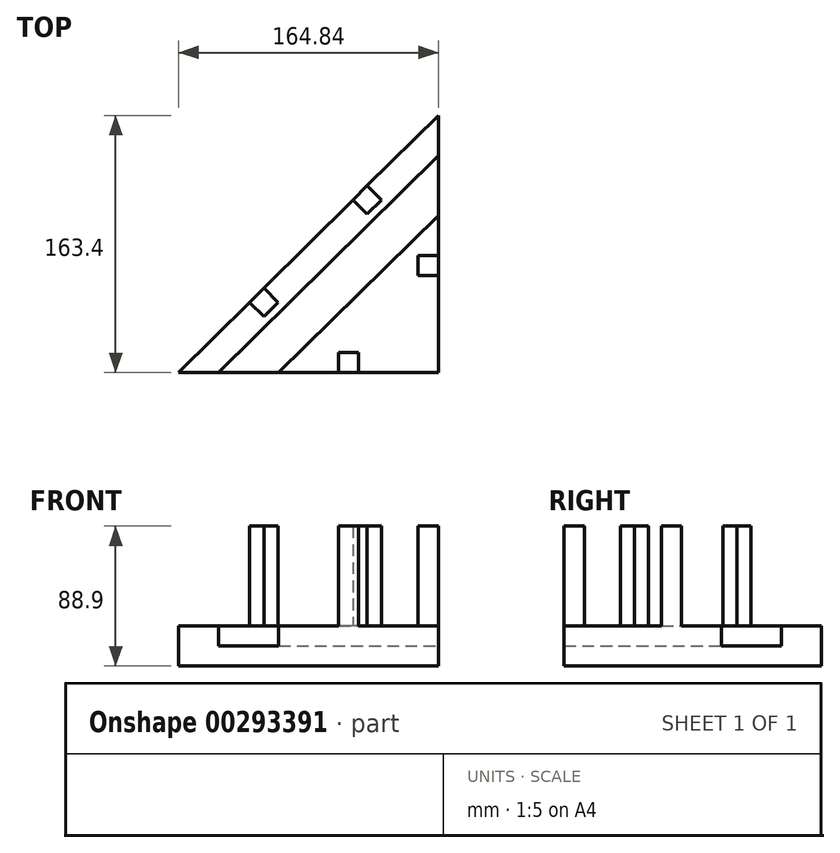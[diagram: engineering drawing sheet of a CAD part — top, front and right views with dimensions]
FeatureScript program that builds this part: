
annotation { "Feature Type Name" : "Feature", "Feature Type Description" : "" }
export const myFeature = defineFeature(function(context is Context, id is Id, definition is map)
    precondition{}
    {
        {
            var Q0;
            Q0=qCreatedBy(makeId("Top.planeOp"),FACE);
            var sketch = newSketch(context, id + "F0", { "sketchPlane" : qUnion([Q0])});
            skLineSegment(sketch, "E0.top", {"start": v(82.42, -81.7) * mm, "end": v(-82.42, -81.7) * mm});
            skLineSegment(sketch, "E0.left", {"start": v(82.42, 81.7) * mm, "end": v(82.42, -81.7) * mm});
            skPoint(sketch, "E0.middle", {"position": v(0, 0) * mm});
            skLineSegment(sketch, "E1", {"start": v(82.42, 81.7) * mm, "end": v(-82.42, -81.7) * mm});
            skSolve(sketch);
        }
        {
            var Q0;
            Q0=makeQuery(id+"F0.imprint","IMPRINT",FACE,{"disambiguationData":[TD([[makeQuery(id+"F0.imprint","IMPRINT",EDGE,{"derivedFrom":sQuery(id+"F0.wireOp",EDGE,"E0.top")}),-1.0]])]});
            extrude(context, id + "F1", {"entities" : qUnion([Q0]), "depth" : 25.4 * mm});
        }
        {
            var Q0;
            Q0=makeQuery(id+"F1.opExtrude","CAP_FACE",FACE,{"disambiguationData":[OSD([sQuery(id+"F0.wireOp",EDGE,"E0.top"),sQuery(id+"F0.wireOp",EDGE,"E0.left"),sQuery(id+"F0.wireOp",EDGE,"E1")])],"isStart":false});
            var sketch = newSketch(context, id + "F2", { "sketchPlane" : qUnion([Q0])});
            skLineSegment(sketch, "E2", {"start": v(-82.42, -81.7) * mm, "end": v(-18.92, -81.7) * mm});
            skLineSegment(sketch, "E3", {"start": v(82.42, 81.7) * mm, "end": v(82.42, 18.2) * mm});
            skLineSegment(sketch, "E4", {"start": v(-18.92, -81.7) * mm, "end": v(82.42, 18.2) * mm});
            skLineSegment(sketch, "E5", {"start": v(-82.42, -81.7) * mm, "end": v(-57.02, -81.7) * mm});
            skLineSegment(sketch, "E6", {"start": v(82.42, 81.7) * mm, "end": v(82.42, 56.3) * mm});
            skLineSegment(sketch, "E7", {"start": v(82.42, 56.3) * mm, "end": v(-57.02, -81.7) * mm});
            skLineSegment(sketch, "E8", {"start": v(-18.92, -81.7) * mm, "end": v(19.18, -81.7) * mm});
            skLineSegment(sketch, "E9", {"start": v(82.42, 18.2) * mm, "end": v(82.42, -19.9) * mm});
            skLineSegment(sketch, "E10", {"start": v(82.42, -19.9) * mm, "end": v(69.72, -19.9) * mm});
            skLineSegment(sketch, "E11", {"start": v(69.72, -19.9) * mm, "end": v(69.72, -7.2) * mm});
            skLineSegment(sketch, "E12", {"start": v(69.72, -7.2) * mm, "end": v(82.42, -7.2) * mm});
            skLineSegment(sketch, "E13", {"start": v(19.18, -81.7) * mm, "end": v(19.18, -69) * mm});
            skLineSegment(sketch, "E14", {"start": v(19.18, -69) * mm, "end": v(31.88, -69) * mm});
            skLineSegment(sketch, "E15", {"start": v(31.88, -69) * mm, "end": v(31.88, -81.7) * mm});
            skLineSegment(sketch, "E16", {"start": v(-82.42, -81.7) * mm, "end": v(-31.62, -81.7) * mm});
            skLineSegment(sketch, "E17", {"start": v(82.42, 81.7) * mm, "end": v(82.42, 30.9) * mm});
            skLineSegment(sketch, "E18", {"start": v(-82.42, -81.7) * mm, "end": v(-37.32, -37) * mm});
            skLineSegment(sketch, "E19", {"start": v(82.42, 81.7) * mm, "end": v(37.32, 37) * mm});
            skLineSegment(sketch, "E20", {"start": v(37.32, 37) * mm, "end": v(46.26, 27.97) * mm});
            skLineSegment(sketch, "E21", {"start": v(46.26, 27.97) * mm, "end": v(37.24, 19.03) * mm});
            skLineSegment(sketch, "E22", {"start": v(37.24, 19.03) * mm, "end": v(28.3, 28.05) * mm});
            skLineSegment(sketch, "E23", {"start": v(-37.32, -37) * mm, "end": v(-28.38, -46.01) * mm});
            skLineSegment(sketch, "E24", {"start": v(-28.38, -46.01) * mm, "end": v(-19.35, -37.08) * mm});
            skLineSegment(sketch, "E25", {"start": v(-19.35, -37.08) * mm, "end": v(-28.38, -27.96) * mm});
            skLineSegment(sketch, "E26", {"start": v(82.42, 81.7) * mm, "end": v(82.42, 43.6) * mm});
            skSolve(sketch);
        }
        {
            var Q0;
            {var subQ0=sQuery(id+"F2.wireOp",EDGE,"E20");Q0=makeQuery(id+"F2.imprint","IMPRINT",FACE,{"disambiguationData":[TD([[makeQuery(id+"F2.imprint","IMPRINT",EDGE,{"derivedFrom":subQ0}),-1.0]])]});}
            var Q1;
            Q1=makeQuery(id+"F2.imprint","IMPRINT",FACE,{"disambiguationData":[TD([[makeQuery(id+"F2.imprint","IMPRINT",EDGE,{"derivedFrom":sQuery(id+"F2.wireOp",EDGE,"E3")}),-1.0]])]});
            var Q2;
            {var subQ0=sQuery(id+"F2.wireOp",EDGE,"E10");Q2=makeQuery(id+"F2.imprint","IMPRINT",FACE,{"disambiguationData":[TD([[makeQuery(id+"F2.imprint","IMPRINT",EDGE,{"derivedFrom":subQ0}),-1.0]])]});}
            var Q3;
            {var subQ0=sQuery(id+"F2.wireOp",EDGE,"E13");Q3=makeQuery(id+"F2.imprint","IMPRINT",FACE,{"disambiguationData":[TD([[makeQuery(id+"F2.imprint","IMPRINT",EDGE,{"derivedFrom":subQ0}),-1.0]])]});}
            var Q4;
            Q4=makeQuery(id+"F2.imprint","IMPRINT",FACE,{"disambiguationData":[TD([[makeQuery(id+"F2.imprint","IMPRINT",EDGE,{"derivedFrom":sQuery(id+"F2.wireOp",EDGE,"E2")}),-1.0]])]});
            var Q5;
            {var subQ0=sQuery(id+"F2.wireOp",EDGE,"E23");Q5=makeQuery(id+"F2.imprint","IMPRINT",FACE,{"disambiguationData":[TD([[makeQuery(id+"F2.imprint","IMPRINT",EDGE,{"derivedFrom":subQ0}),1.0]])]});}
            extrude(context, id + "F3", {"entities" : qUnion([Q0, Q1, Q2, Q3, Q4, Q5]), "operationType" : NewBodyOperationType.ADD, "depth" : 63.5 * mm});
        }
        {
            var Q0;
            Q0=makeQuery(id+"F3.opExtrude","CAP_FACE",FACE,{"disambiguationData":[OSD([sQuery(id+"F2.wireOp",EDGE,"E2"),sQuery(id+"F2.wireOp",EDGE,"E3"),sQuery(id+"F2.wireOp",EDGE,"E4"),sQuery(id+"F2.wireOp",EDGE,"E7"),sQuery(id+"F2.wireOp",EDGE,"E16"),sQuery(id+"F2.wireOp",EDGE,"E17"),sQuery(id+"F2.wireOp",EDGE,"E26")])],"isStart":false});
            extrude(context, id + "F4", {"entities" : qUnion([Q0]), "operationType" : NewBodyOperationType.REMOVE, "oppositeDirection" : true, "depth" : 76.2 * mm});
        }
        {
            var Q0;
            {var subQ0=sQuery(id+"F0.wireOp",EDGE,"E0.top");var subQ1=sQuery(id+"F0.wireOp",EDGE,"E0.left");Q0=makeQuery(id+"F3.boolean.opBoolean","SPLIT",FACE,{"disambiguationData":[TD([makeQuery(id+"F3.opExtrude","SWEPT_FACE",FACE,{"disambiguationData":[OSD([sQuery(id+"F2.wireOp",EDGE,"E4")])]})])],"derivedFrom":makeQuery(id+"F1.opExtrude","CAP_FACE",FACE,{"disambiguationData":[OSD([subQ0,subQ1,sQuery(id+"F0.wireOp",EDGE,"E1")])],"isStart":false})});}
            var sketch = newSketch(context, id + "F5", { "sketchPlane" : qUnion([Q0])});
            skLineSegment(sketch, "E27", {"start": v(-18.92, -81.7) * mm, "end": v(-8.76, -81.7) * mm});
            skLineSegment(sketch, "E28", {"start": v(-8.76, -81.7) * mm, "end": v(82.42, 8.18) * mm});
            skSolve(sketch);
        }
        {
            var Q0;
            Q0=makeQuery(id+"F5.imprint","IMPRINT",FACE,{"disambiguationData":[TD([[makeQuery(id+"F5.imprint","IMPRINT",EDGE,{"derivedFrom":sQuery(id+"F5.wireOp",EDGE,"E27")}),-1.0]])]});
            extrude(context, id + "F6", {"entities" : qUnion([Q0]), "operationType" : NewBodyOperationType.ADD, "oppositeDirection" : true, "depth" : 12.7 * mm});
        }
    });
